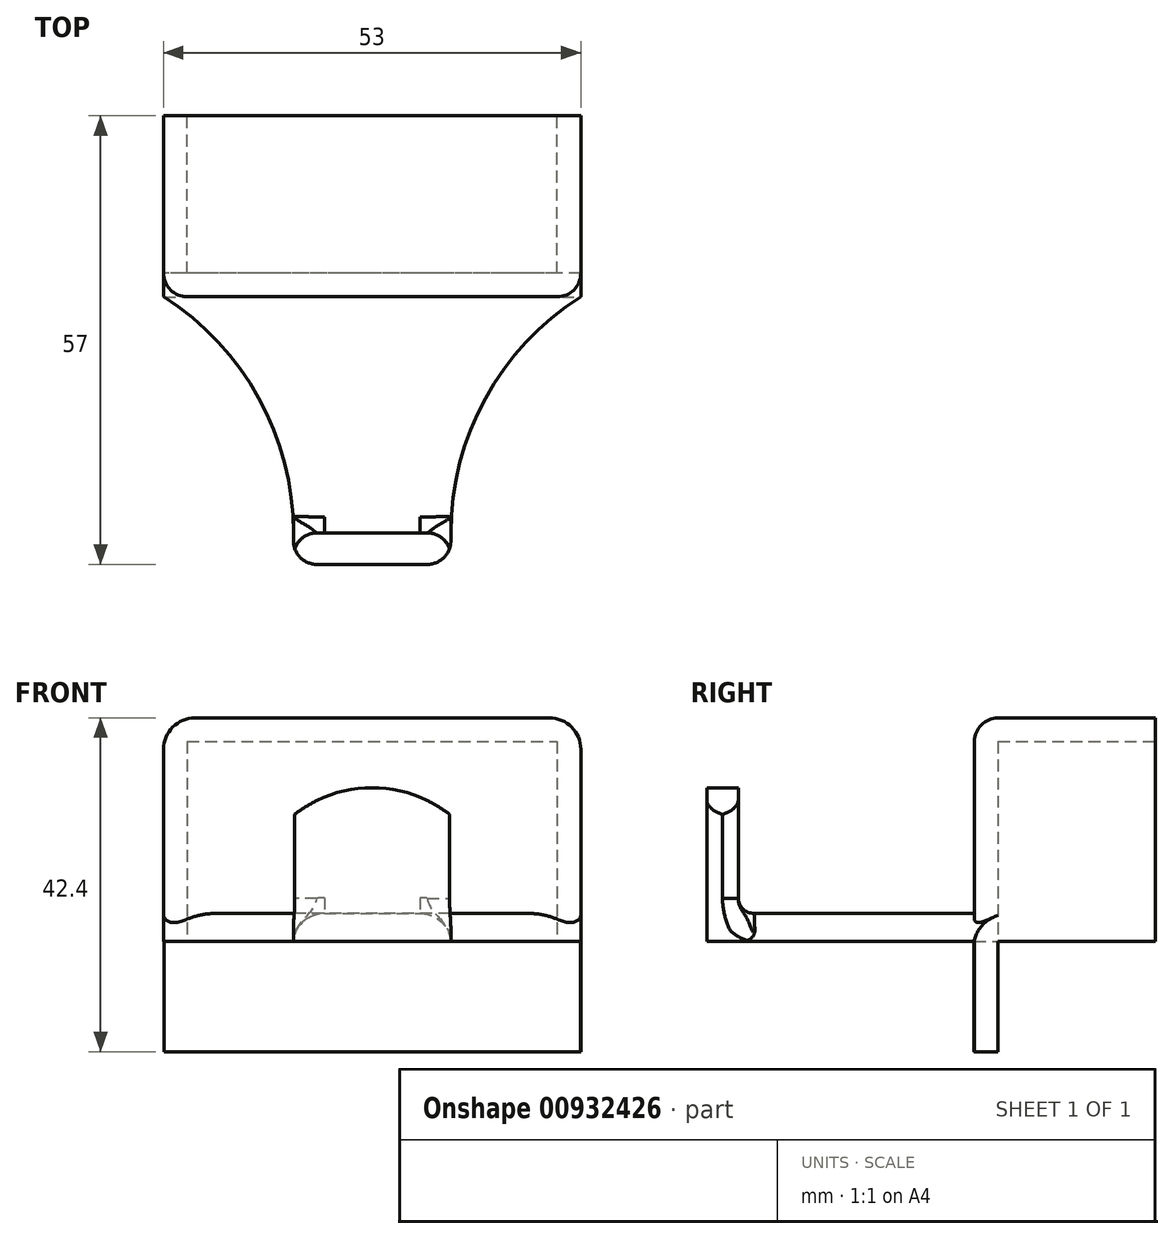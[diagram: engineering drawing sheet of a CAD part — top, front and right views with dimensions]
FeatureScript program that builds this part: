
annotation { "Feature Type Name" : "Feature", "Feature Type Description" : "" }
export const myFeature = defineFeature(function(context is Context, id is Id, definition is map)
    precondition{}
    {
        {
            var Q0;
            Q0=qCreatedBy(makeId("Top.planeOp"),FACE);
            var sketch = newSketch(context, id + "F0", { "sketchPlane" : qUnion([Q0])});
            skLineSegment(sketch, "E0.bottom", {"start": v(26.5, -11.5) * mm, "end": v(-26.5, -11.5) * mm});
            skLineSegment(sketch, "E0.top", {"start": v(26.5, 11.5) * mm, "end": v(23.5, 11.5) * mm});
            skLineSegment(sketch, "E0.left", {"start": v(26.5, -11.5) * mm, "end": v(26.5, 11.5) * mm});
            skLineSegment(sketch, "E0.right", {"start": v(-26.5, -11.5) * mm, "end": v(-26.5, 11.5) * mm});
            skPoint(sketch, "E0.middle", {"position": v(0, 0) * mm});
            skLineSegment(sketch, "E1", {"start": v(-10, -41.5) * mm, "end": v(10, -41.5) * mm});
            skLineSegment(sketch, "E2.0", {"start": v(-23.5, -8.5) * mm, "end": v(-23.5, 11.5) * mm});
            skLineSegment(sketch, "E3.0", {"start": v(23.5, -8.5) * mm, "end": v(23.5, 11.5) * mm});
            skLineSegment(sketch, "E4.0", {"start": v(23.5, -8.5) * mm, "end": v(-23.5, -8.5) * mm});
            skLineSegment(sketch, "E5.trimOffspring", {"start": v(-23.5, 11.5) * mm, "end": v(-26.5, 11.5) * mm});
            skLineSegment(sketch, "E6.top", {"start": v(-10, -45.5) * mm, "end": v(10, -45.5) * mm});
            skLineSegment(sketch, "E6.left", {"start": v(-10, -41.5) * mm, "end": v(-10, -45.5) * mm});
            skLineSegment(sketch, "E6.right", {"start": v(10, -41.5) * mm, "end": v(10, -45.5) * mm});
            skArc(sketch, "E7", {"start": v(-10, -41.5) * mm, "mid": v(-14.4, -24.38) * mm, "end": v(-26.5, -11.5) * mm});
            skArc(sketch, "E8", {"start": v(26.5, -11.5) * mm, "mid": v(14.4, -24.38) * mm, "end": v(10, -41.5) * mm});
            skLineSegment(sketch, "E9", {"start": v(0, -11.5) * mm, "end": v(0, -41.5) * mm});
            skSolve(sketch);
        }
        {
            var Q0;
            Q0=makeQuery(id+"F0.imprint","IMPRINT",FACE,{"disambiguationData":[TD([[makeQuery(id+"F0.imprint","IMPRINT",EDGE,{"derivedFrom":sQuery(id+"F0.wireOp",EDGE,"E0.bottom")}),1.0]])]});
            extrude(context, id + "F1", {"entities" : qUnion([Q0]), "depth" : 3.56 * mm, "offsetDistance" : 25.4 * mm});
        }
        {
            var Q0;
            Q0=makeQuery(id+"F0.imprint","IMPRINT",FACE,{"disambiguationData":[TD([[makeQuery(id+"F0.imprint","IMPRINT",EDGE,{"derivedFrom":sQuery(id+"F0.wireOp",EDGE,"E6.top")}),1.0]])]});
            extrude(context, id + "F2", {"entities" : qUnion([Q0]), "operationType" : NewBodyOperationType.ADD, "depth" : 16 * mm, "offsetDistance" : 25.4 * mm});
        }
        {
            var Q0;
            Q0=makeQuery(id+"F0.imprint","IMPRINT",FACE,{"disambiguationData":[TD([[makeQuery(id+"F0.imprint","IMPRINT",EDGE,{"derivedFrom":sQuery(id+"F0.wireOp",EDGE,"E0.bottom")}),-1.0]])]});
            extrude(context, id + "F3", {"entities" : qUnion([Q0]), "operationType" : NewBodyOperationType.ADD, "depth" : 25.4 * mm, "offsetDistance" : 25.4 * mm});
        }
        {
            var Q0;
            Q0=makeQuery(id+"F3.opExtrude","CAP_FACE",FACE,{"disambiguationData":[OSD([sQuery(id+"F0.wireOp",EDGE,"E0.bottom"),sQuery(id+"F0.wireOp",EDGE,"E0.top"),sQuery(id+"F0.wireOp",EDGE,"E0.left"),sQuery(id+"F0.wireOp",EDGE,"E0.right"),sQuery(id+"F0.wireOp",EDGE,"E2.0"),sQuery(id+"F0.wireOp",EDGE,"E3.0"),sQuery(id+"F0.wireOp",EDGE,"E4.0"),sQuery(id+"F0.wireOp",EDGE,"E5.trimOffspring")])],"isStart":false});
            var sketch = newSketch(context, id + "F4", { "sketchPlane" : qUnion([Q0])});
            skLineSegment(sketch, "E10.bottom", {"start": v(-26.5, 11.5) * mm, "end": v(26.5, 11.5) * mm});
            skLineSegment(sketch, "E10.top", {"start": v(-26.5, -11.5) * mm, "end": v(26.5, -11.5) * mm});
            skLineSegment(sketch, "E10.left", {"start": v(-26.5, 11.5) * mm, "end": v(-26.5, -11.5) * mm});
            skLineSegment(sketch, "E10.right", {"start": v(26.5, 11.5) * mm, "end": v(26.5, -11.5) * mm});
            skLineSegment(sketch, "E11.bottom", {"start": v(26.5, 11.5) * mm, "end": v(-26.5, 11.5) * mm});
            skLineSegment(sketch, "E11.top", {"start": v(26.5, -11.5) * mm, "end": v(-26.5, -11.5) * mm});
            skSolve(sketch);
        }
        {
            var Q0;
            Q0 = qSketchRegion(id + "F4", true);
            extrude(context, id + "F5", {"entities" : qUnion([Q0]), "operationType" : NewBodyOperationType.ADD, "depth" : 3 * mm, "offsetDistance" : 25 * mm});
        }
        {
            var Q0;
            Q0=makeQuery(id+"F1.opExtrude","CAP_EDGE",EDGE,{"disambiguationData":[OSD([sQuery(id+"F0.wireOp",EDGE,"E8")])],"isStart":false});
            var Q1;
            Q1=makeQuery(id+"F5.opExtrude","CAP_EDGE",EDGE,{"disambiguationData":[OSD([sQuery(id+"F4.wireOp",EDGE,"E10.right")])],"isStart":false});
            var Q2;
            Q2=makeQuery(id+"F5.opExtrude","CAP_EDGE",EDGE,{"disambiguationData":[OSD([sQuery(id+"F4.wireOp",EDGE,"E10.left")])],"isStart":false});
            var Q3;
            Q3=makeQuery(id+"F1.opExtrude","CAP_EDGE",EDGE,{"disambiguationData":[OSD([sQuery(id+"F0.wireOp",EDGE,"E7")])],"isStart":false});
            fillet(context, id + "F6", {"entities" : qUnion([Q0, Q1, Q2, Q3]), "radius" : 4 * mm, "tangentPropagation" : true, "allowEdgeOverflow" : false});
        }
        {
            var Q0;
            Q0=makeQuery(id+"F6.opFillet","BLEND_EDGE",EDGE,{"blendedFrom":[makeQuery(id+"F1.opExtrude","CAP_EDGE",EDGE,{"disambiguationData":[OSD([sQuery(id+"F0.wireOp",EDGE,"E8")])],"isStart":false}),makeQuery(id+"F2.opExtrude","SWEPT_FACE",FACE,{"disambiguationData":[OSD([sQuery(id+"F0.wireOp",EDGE,"E1")])]})],"blendedInto":[makeQuery(id+"F2.opExtrude","SWEPT_FACE",FACE,{"disambiguationData":[OSD([sQuery(id+"F0.wireOp",EDGE,"E1")])]})]});
            var Q1;
            Q1=makeQuery(id+"F1.opExtrude","CAP_EDGE",EDGE,{"disambiguationData":[OSD([sQuery(id+"F0.wireOp",EDGE,"E0.bottom")])],"isStart":false});
            fillet(context, id + "F7", {"entities" : qUnion([Q0, Q1]), "radius" : 2 * mm, "tangentPropagation" : true, "allowEdgeOverflow" : false});
        }
        {
            var Q0;
            Q0=makeQuery(id+"F2.opExtrude","SWEPT_FACE",FACE,{"disambiguationData":[OSD([sQuery(id+"F0.wireOp",EDGE,"E6.top")])]});
            var sketch = newSketch(context, id + "F8", { "sketchPlane" : qUnion([Q0])});
            skArc(sketch, "E12", {"start": v(10, 16) * mm, "mid": v(0, 19.53) * mm, "end": v(-10, 16) * mm});
            skSolve(sketch);
        }
        {
            var Q0;
            Q0=makeQuery(id+"F8.imprint","IMPRINT",FACE,{"disambiguationData":[TD([[makeQuery(id+"F8.imprint","IMPRINT",EDGE,{"derivedFrom":sQuery(id+"F8.wireOp",EDGE,"E12")}),1.0]])]});
            extrude(context, id + "F9", {"entities" : qUnion([Q0]), "operationType" : NewBodyOperationType.ADD, "oppositeDirection" : true, "depth" : 4 * mm, "offsetDistance" : 25 * mm});
        }
        {
            var Q0;
            {var subQ0=sQuery(id+"F0.wireOp",EDGE,"E6.right");Q0=makeQuery(id+"F9.boolean.opBoolean","MERGE",EDGE,{"derivedFrom":[makeQuery(id+"F2.opExtrude","CAP_EDGE",EDGE,{"disambiguationData":[OSD([subQ0])],"isStart":false}),makeQuery(id+"F9.opExtrude","SWEPT_EDGE",EDGE,{"disambiguationData":[OSD([sQuery(id+"F0.wireOp",EDGE,"E6.top"),subQ0,sQuery(id+"F8.wireOp",EDGE,"E12")])]})]});}
            var Q1;
            {var subQ0=sQuery(id+"F0.wireOp",EDGE,"E6.left");Q1=makeQuery(id+"F9.boolean.opBoolean","MERGE",EDGE,{"derivedFrom":[makeQuery(id+"F2.opExtrude","CAP_EDGE",EDGE,{"disambiguationData":[OSD([subQ0])],"isStart":false}),makeQuery(id+"F9.opExtrude","SWEPT_EDGE",EDGE,{"disambiguationData":[OSD([sQuery(id+"F0.wireOp",EDGE,"E6.top"),subQ0,sQuery(id+"F8.wireOp",EDGE,"E12")])]})]});}
            var Q2;
            {var subQ0=sQuery(id+"F0.wireOp",EDGE,"E8");var subQ1=sQuery(id+"F0.wireOp",EDGE,"E0.left");var subQ2=sQuery(id+"F0.wireOp",EDGE,"E0.bottom");var subQ3=makeQuery(id+"F3.opExtrude","SWEPT_EDGE",EDGE,{"disambiguationData":[OSD([subQ2,subQ1,subQ0])]});Q2=makeQuery(id+"F6.opFillet","MERGE",EDGE,{"derivedFrom":[makeQuery(id+"F3.boolean.opBoolean","MERGE",EDGE,{"derivedFrom":[makeQuery(id+"F1.opExtrude","SWEPT_EDGE",EDGE,{"disambiguationData":[OSD([subQ2,subQ1,subQ0])]}),subQ3]}),makeQuery(id+"F5.boolean.opBoolean","MERGE",EDGE,{"derivedFrom":[makeQuery(id+"F3.boolean.opBoolean","SPLIT",EDGE,{"derivedFrom":subQ3}),makeQuery(id+"F5.opExtrude","SWEPT_EDGE",EDGE,{"disambiguationData":[OSD([sQuery(id+"F4.wireOp",EDGE,"E11.top"),sQuery(id+"F4.wireOp",EDGE,"E10.right")])]})]})]});}
            var Q3;
            {var subQ0=sQuery(id+"F0.wireOp",EDGE,"E8");var subQ1=sQuery(id+"F0.wireOp",EDGE,"E6.right");var subQ2=sQuery(id+"F0.wireOp",EDGE,"E1");var subQ3=makeQuery(id+"F2.opExtrude","SWEPT_EDGE",EDGE,{"disambiguationData":[OSD([subQ2,subQ1,subQ0])]});Q3=makeQuery(id+"F6.opFillet","MERGE",EDGE,{"derivedFrom":[makeQuery(id+"F2.boolean.opBoolean","MERGE",EDGE,{"derivedFrom":[makeQuery(id+"F1.opExtrude","SWEPT_EDGE",EDGE,{"disambiguationData":[OSD([subQ2,subQ1,subQ0])]}),subQ3]}),makeQuery(id+"F2.boolean.opBoolean","SPLIT",EDGE,{"derivedFrom":subQ3})]});}
            var Q4;
            Q4=makeQuery(id+"F2.opExtrude","SWEPT_EDGE",EDGE,{"disambiguationData":[OSD([sQuery(id+"F0.wireOp",EDGE,"E6.top"),sQuery(id+"F0.wireOp",EDGE,"E6.right")])]});
            var Q5;
            Q5=makeQuery(id+"F2.opExtrude","SWEPT_EDGE",EDGE,{"disambiguationData":[OSD([sQuery(id+"F0.wireOp",EDGE,"E6.top"),sQuery(id+"F0.wireOp",EDGE,"E6.left")])]});
            var Q6;
            {var subQ0=sQuery(id+"F0.wireOp",EDGE,"E7");var subQ1=sQuery(id+"F0.wireOp",EDGE,"E6.left");var subQ2=sQuery(id+"F0.wireOp",EDGE,"E1");var subQ3=makeQuery(id+"F2.opExtrude","SWEPT_EDGE",EDGE,{"disambiguationData":[OSD([subQ2,subQ1,subQ0])]});Q6=makeQuery(id+"F6.opFillet","MERGE",EDGE,{"derivedFrom":[makeQuery(id+"F2.boolean.opBoolean","MERGE",EDGE,{"derivedFrom":[makeQuery(id+"F1.opExtrude","SWEPT_EDGE",EDGE,{"disambiguationData":[OSD([subQ2,subQ1,subQ0])]}),subQ3]}),makeQuery(id+"F2.boolean.opBoolean","SPLIT",EDGE,{"derivedFrom":subQ3})]});}
            fillet(context, id + "F10", {"entities" : qUnion([Q0, Q1, Q2, Q3, Q4, Q5, Q6]), "radius" : 3 * mm, "tangentPropagation" : true, "allowEdgeOverflow" : false});
        }
        {
            var Q0;
            {var subQ0=sQuery(id+"F0.wireOp",EDGE,"E0.bottom");var subQ1=sQuery(id+"F0.wireOp",EDGE,"E1");Q0=makeQuery(id+"F3.boolean.opBoolean","MERGE",FACE,{"derivedFrom":[makeQuery(id+"F2.boolean.opBoolean","MERGE",FACE,{"derivedFrom":[makeQuery(id+"F1.opExtrude","CAP_FACE",FACE,{"disambiguationData":[OSD([subQ0,subQ1,sQuery(id+"F0.wireOp",EDGE,"E7"),sQuery(id+"F0.wireOp",EDGE,"E8")])],"isStart":true}),makeQuery(id+"F2.opExtrude","CAP_FACE",FACE,{"disambiguationData":[OSD([subQ1,sQuery(id+"F0.wireOp",EDGE,"E6.top"),sQuery(id+"F0.wireOp",EDGE,"E6.left"),sQuery(id+"F0.wireOp",EDGE,"E6.right")])],"isStart":true})]}),makeQuery(id+"F3.opExtrude","CAP_FACE",FACE,{"disambiguationData":[OSD([subQ0,sQuery(id+"F0.wireOp",EDGE,"E0.top"),sQuery(id+"F0.wireOp",EDGE,"E0.left"),sQuery(id+"F0.wireOp",EDGE,"E0.right"),sQuery(id+"F0.wireOp",EDGE,"E2.0"),sQuery(id+"F0.wireOp",EDGE,"E3.0"),sQuery(id+"F0.wireOp",EDGE,"E4.0"),sQuery(id+"F0.wireOp",EDGE,"E5.trimOffspring")])],"isStart":true})]});}
            var sketch = newSketch(context, id + "F11", { "sketchPlane" : qUnion([Q0])});
            skLineSegment(sketch, "E13.bottom", {"start": v(-26.44, 11.53) * mm, "end": v(26.5, 11.53) * mm});
            skLineSegment(sketch, "E13.top", {"start": v(-26.44, 8.5) * mm, "end": v(26.5, 8.5) * mm});
            skLineSegment(sketch, "E13.left", {"start": v(-26.44, 11.53) * mm, "end": v(-26.44, 8.5) * mm});
            skLineSegment(sketch, "E13.right", {"start": v(26.5, 11.53) * mm, "end": v(26.5, 8.5) * mm});
            skSolve(sketch);
        }
        {
            var Q0;
            {var subQ0=sQuery(id+"F11.wireOp",EDGE,"E13.top");var subQ1=sQuery(id+"F0.wireOp",EDGE,"E3.0");var subQ2=makeQuery(id+"F11.imprint","INTERSECT",VERTEX,{"derivedFrom":[makeQuery(id+"F3.opExtrude","CAP_EDGE",EDGE,{"disambiguationData":[OSD([subQ1])],"isStart":true}),subQ0]});var subQ7=sQuery(id+"F0.wireOp",EDGE,"E2.0");var subQ19=makeQuery(id+"F11.imprint","INTERSECT",VERTEX,{"derivedFrom":[makeQuery(id+"F3.opExtrude","CAP_EDGE",EDGE,{"disambiguationData":[OSD([subQ7])],"isStart":true}),subQ0]});Q0=makeQuery(id+"F11.imprint","IMPRINT",FACE,{"disambiguationData":[TD([[makeQuery(id+"F11.imprint","IMPRINT",EDGE,{"disambiguationData":[TD([[subQ19,1.0],[subQ2,-1.0]])],"derivedFrom":subQ0}),-1.0]])]});}
            extrude(context, id + "F12", {"entities" : qUnion([Q0]), "operationType" : NewBodyOperationType.ADD, "depth" : 14 * mm, "offsetDistance" : 25 * mm});
        }
    });
